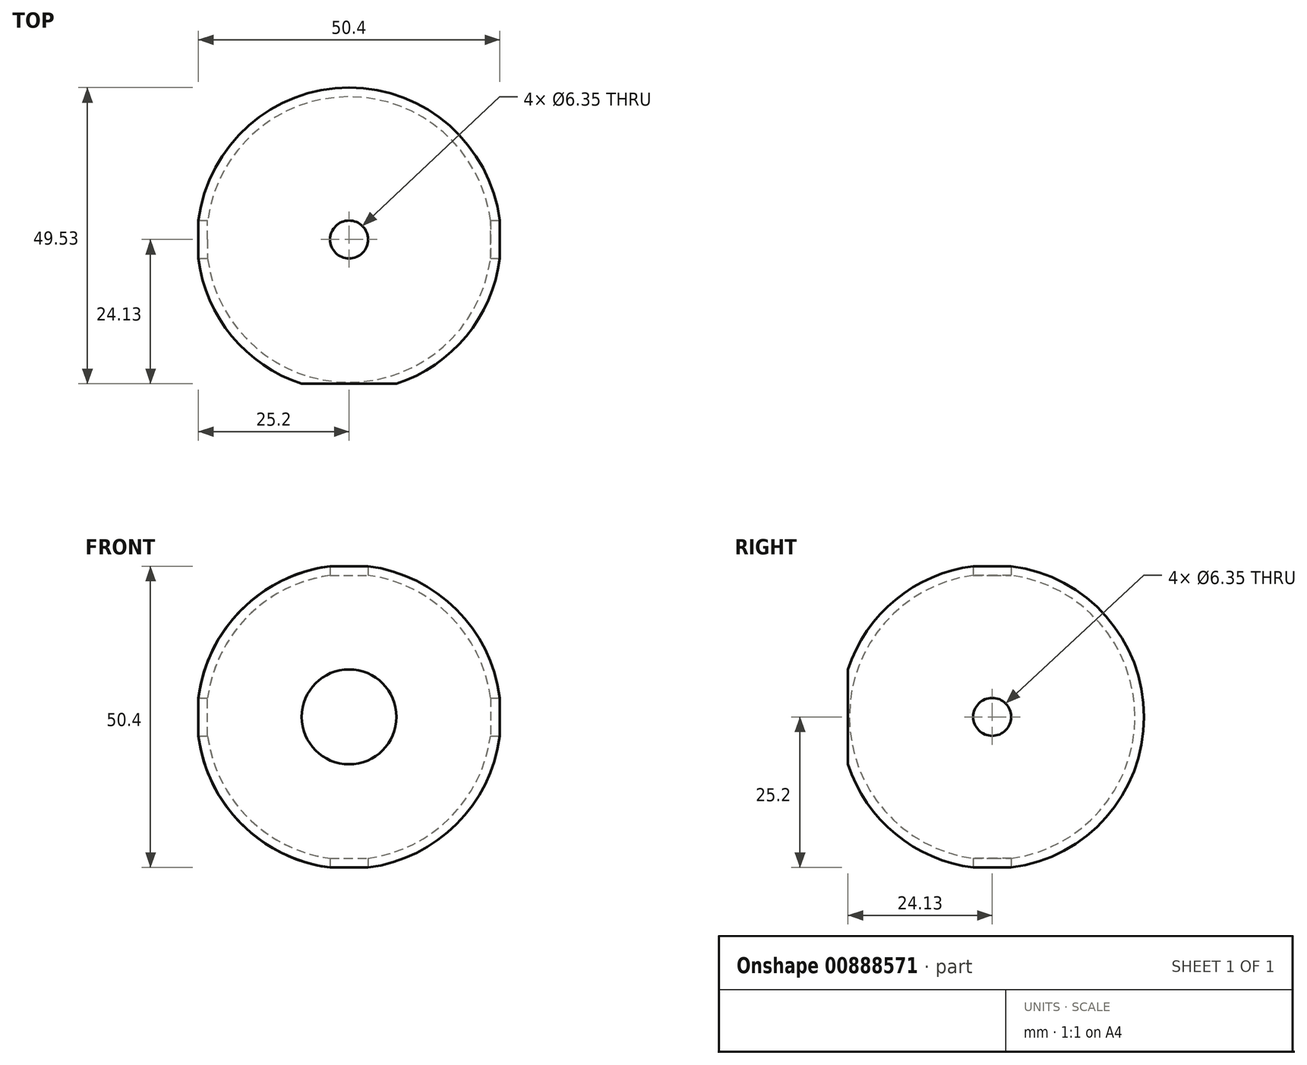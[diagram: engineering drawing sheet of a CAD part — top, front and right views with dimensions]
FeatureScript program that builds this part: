
annotation { "Feature Type Name" : "Feature", "Feature Type Description" : "" }
export const myFeature = defineFeature(function(context is Context, id is Id, definition is map)
    precondition{}
    {
        {
            var Q0;
            Q0=qCreatedBy(makeId("Front.planeOp"),FACE);
            var sketch = newSketch(context, id + "F0", { "sketchPlane" : qUnion([Q0])});
            skLineSegment(sketch, "E0", {"start": v(0, 0) * mm, "end": v(0, 53.8) * mm, "construction": true});
            skArc(sketch, "E1", {"start": v(3.18, -23.66) * mm, "mid": v(23.88, 0) * mm, "end": v(3.18, 23.66) * mm});
            skArc(sketch, "E2.0", {"start": v(3.18, -25.2) * mm, "mid": v(25.4, 0) * mm, "end": v(3.18, 25.2) * mm});
            skLineSegment(sketch, "E3", {"start": v(3.18, 23.66) * mm, "end": v(3.18, 25.2) * mm});
            skLineSegment(sketch, "E4", {"start": v(3.18, -23.66) * mm, "end": v(3.18, -25.2) * mm});
            skSolve(sketch);
        }
        {
            var Q0;
            Q0 = qSketchRegion(id + "F0", true);
            var Q1;
            Q1=sQuery(id+"F0.wireOp",EDGE,"E0");
            revolve(context, id + "F1", {"surfaceOperationType" : NewSurfaceOperationType.NEW, "entities" : qUnion([Q0]), "axis" : qUnion([Q1]), "revolveType" : RevolveType.FULL});
        }
        {
            var Q0;
            Q0=qCreatedBy(makeId("Right.planeOp"),FACE);
            var sketch = newSketch(context, id + "F2", { "sketchPlane" : qUnion([Q0])});
            skCircle(sketch, "E5", {"center": v(0, 0) * mm, "radius": 3.18 * mm});
            skSolve(sketch);
        }
        {
            var Q0;
            Q0 = qSketchRegion(id + "F2", true);
            extrude(context, id + "F3", {"entities" : qUnion([Q0]), "operationType" : NewBodyOperationType.REMOVE, "endBound" : BoundingType.THROUGH_ALL, "oppositeDirection" : true, "depth" : 25.4 * mm, "offsetDistance" : 25.4 * mm, "hasSecondDirection" : true, "secondDirectionBound" : SecondDirectionBoundingType.THROUGH_ALL, "secondDirectionOppositeDirection" : false, "secondDirectionDepth" : 25.4 * mm});
        }
        {
            var Q0;
            Q0=qCreatedBy(makeId("Right.planeOp"),FACE);
            var sketch = newSketch(context, id + "F4", { "sketchPlane" : qUnion([Q0])});
            skLineSegment(sketch, "E6.bottom", {"start": v(-24.13, -31.09) * mm, "end": v(-30, -31.09) * mm});
            skLineSegment(sketch, "E6.top", {"start": v(-24.13, 31.19) * mm, "end": v(-30, 31.19) * mm});
            skLineSegment(sketch, "E6.left", {"start": v(-24.13, -31.09) * mm, "end": v(-24.13, 31.19) * mm});
            skLineSegment(sketch, "E6.right", {"start": v(-30, -31.09) * mm, "end": v(-30, 31.19) * mm});
            skSolve(sketch);
        }
        {
            var Q0;
            Q0 = qSketchRegion(id + "F4", true);
            extrude(context, id + "F5", {"entities" : qUnion([Q0]), "operationType" : NewBodyOperationType.REMOVE, "endBound" : BoundingType.THROUGH_ALL, "oppositeDirection" : true, "depth" : 25.4 * mm, "offsetDistance" : 25.4 * mm, "hasSecondDirection" : true, "secondDirectionBound" : SecondDirectionBoundingType.THROUGH_ALL, "secondDirectionOppositeDirection" : false, "secondDirectionDepth" : 25.4 * mm});
        }
    });
